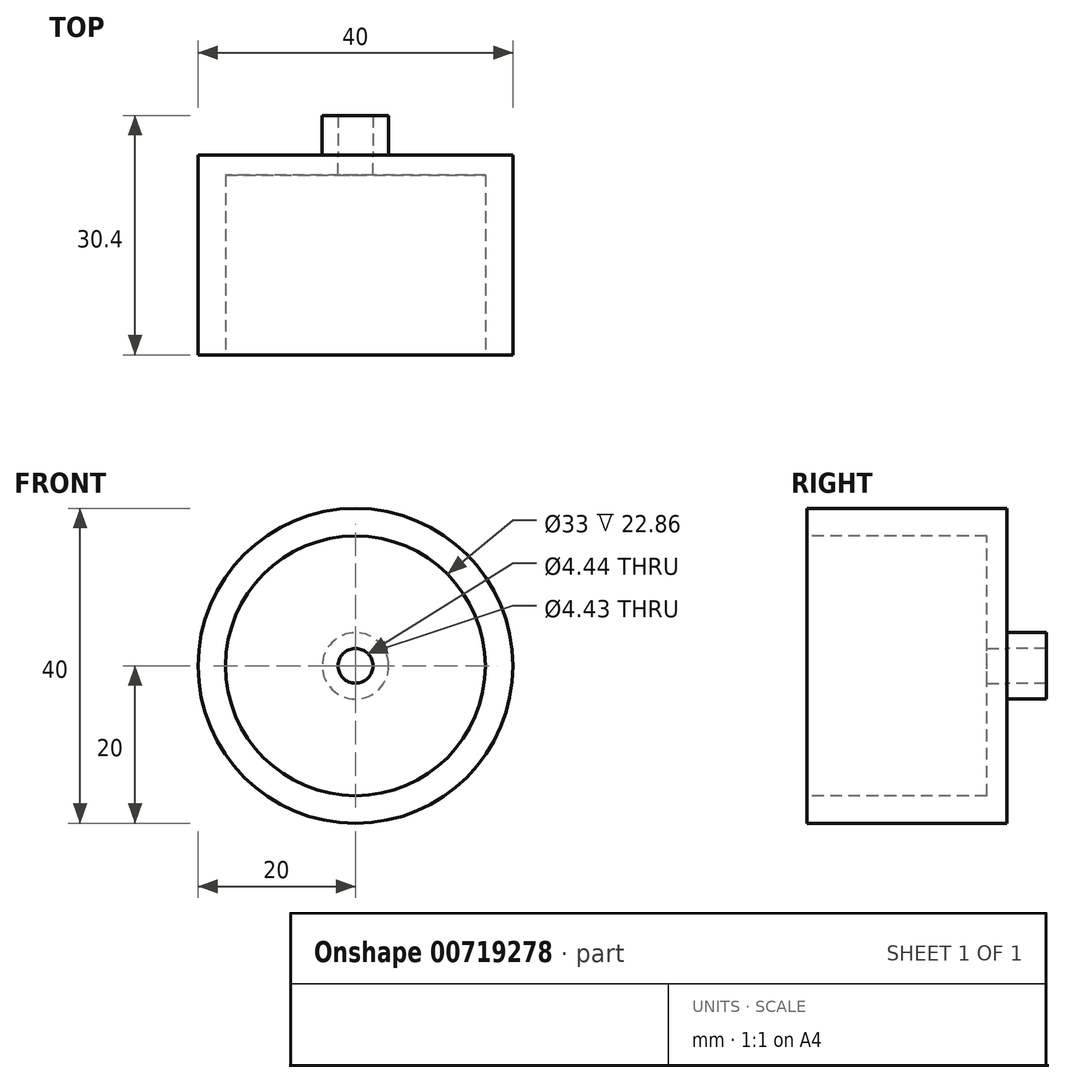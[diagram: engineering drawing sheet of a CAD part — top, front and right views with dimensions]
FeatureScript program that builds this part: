
annotation { "Feature Type Name" : "Feature", "Feature Type Description" : "" }
export const myFeature = defineFeature(function(context is Context, id is Id, definition is map)
    precondition{}
    {
        {
            var Q0;
            Q0=qCreatedBy(makeId("Front.planeOp"),FACE);
            var sketch = newSketch(context, id + "F0", { "sketchPlane" : qUnion([Q0])});
            skCircle(sketch, "E0", {"center": v(0, 0) * mm, "radius": 20 * mm});
            skSolve(sketch);
        }
        {
            var Q0;
            Q0=makeQuery(id+"F0.imprint","IMPRINT",FACE,{"disambiguationData":[TD([[makeQuery(id+"F0.imprint","IMPRINT",EDGE,{"derivedFrom":sQuery(id+"F0.wireOp",EDGE,"E0")}),1.0]])]});
            extrude(context, id + "F1", {"entities" : qUnion([Q0]), "depth" : 25.4 * mm, "offsetDistance" : 25 * mm});
        }
        {
            var Q0;
            Q0=makeQuery(id+"F1.opExtrude","CAP_FACE",FACE,{"disambiguationData":[OSD([sQuery(id+"F0.wireOp",EDGE,"E0")])],"isStart":false});
            var sketch = newSketch(context, id + "F2", { "sketchPlane" : qUnion([Q0])});
            skCircle(sketch, "E1", {"center": v(0, 0) * mm, "radius": 16.5 * mm});
            skSolve(sketch);
        }
        {
            var Q0;
            Q0=makeQuery(id+"F2.imprint","IMPRINT",FACE,{"disambiguationData":[TD([[makeQuery(id+"F2.imprint","IMPRINT",EDGE,{"derivedFrom":sQuery(id+"F2.wireOp",EDGE,"E1")}),1.0]])]});
            extrude(context, id + "F3", {"entities" : qUnion([Q0]), "operationType" : NewBodyOperationType.REMOVE, "oppositeDirection" : true, "depth" : 22.86 * mm, "offsetDistance" : 25 * mm});
        }
        {
            var Q0;
            Q0=makeQuery(id+"F0.imprint","IMPRINT",FACE,{"disambiguationData":[TD([[makeQuery(id+"F0.imprint","IMPRINT",EDGE,{"derivedFrom":sQuery(id+"F0.wireOp",EDGE,"E0")}),1.0]])]});
            var sketch = newSketch(context, id + "F4", { "sketchPlane" : qUnion([Q0])});
            skCircle(sketch, "E2", {"center": v(0, 0) * mm, "radius": 2.22 * mm});
            skCircle(sketch, "E3", {"center": v(0, 0) * mm, "radius": 4.22 * mm});
            skSolve(sketch);
        }
        {
            var Q0;
            Q0=makeQuery(id+"F4.imprint","IMPRINT",FACE,{"disambiguationData":[TD([[makeQuery(id+"F4.imprint","IMPRINT",EDGE,{"derivedFrom":sQuery(id+"F4.wireOp",EDGE,"E2")}),-1.0]])]});
            extrude(context, id + "F5", {"entities" : qUnion([Q0]), "operationType" : NewBodyOperationType.ADD, "oppositeDirection" : true, "depth" : 5 * mm, "offsetDistance" : 25 * mm});
        }
        {
            var Q0;
            Q0=makeQuery(id+"F4.imprint","IMPRINT",FACE,{"disambiguationData":[TD([[makeQuery(id+"F4.imprint","IMPRINT",EDGE,{"derivedFrom":sQuery(id+"F4.wireOp",EDGE,"E2")}),1.0]])]});
            var sketch = newSketch(context, id + "F6", { "sketchPlane" : qUnion([Q0])});
            skCircle(sketch, "E4", {"center": v(0, 0) * mm, "radius": 2.21 * mm});
            skSolve(sketch);
        }
        {
            var Q0;
            Q0 = qSketchRegion(id + "F6", true);
            extrude(context, id + "F7", {"entities" : qUnion([Q0]), "operationType" : NewBodyOperationType.REMOVE, "depth" : 2.54 * mm, "offsetDistance" : 25 * mm});
        }
    });
